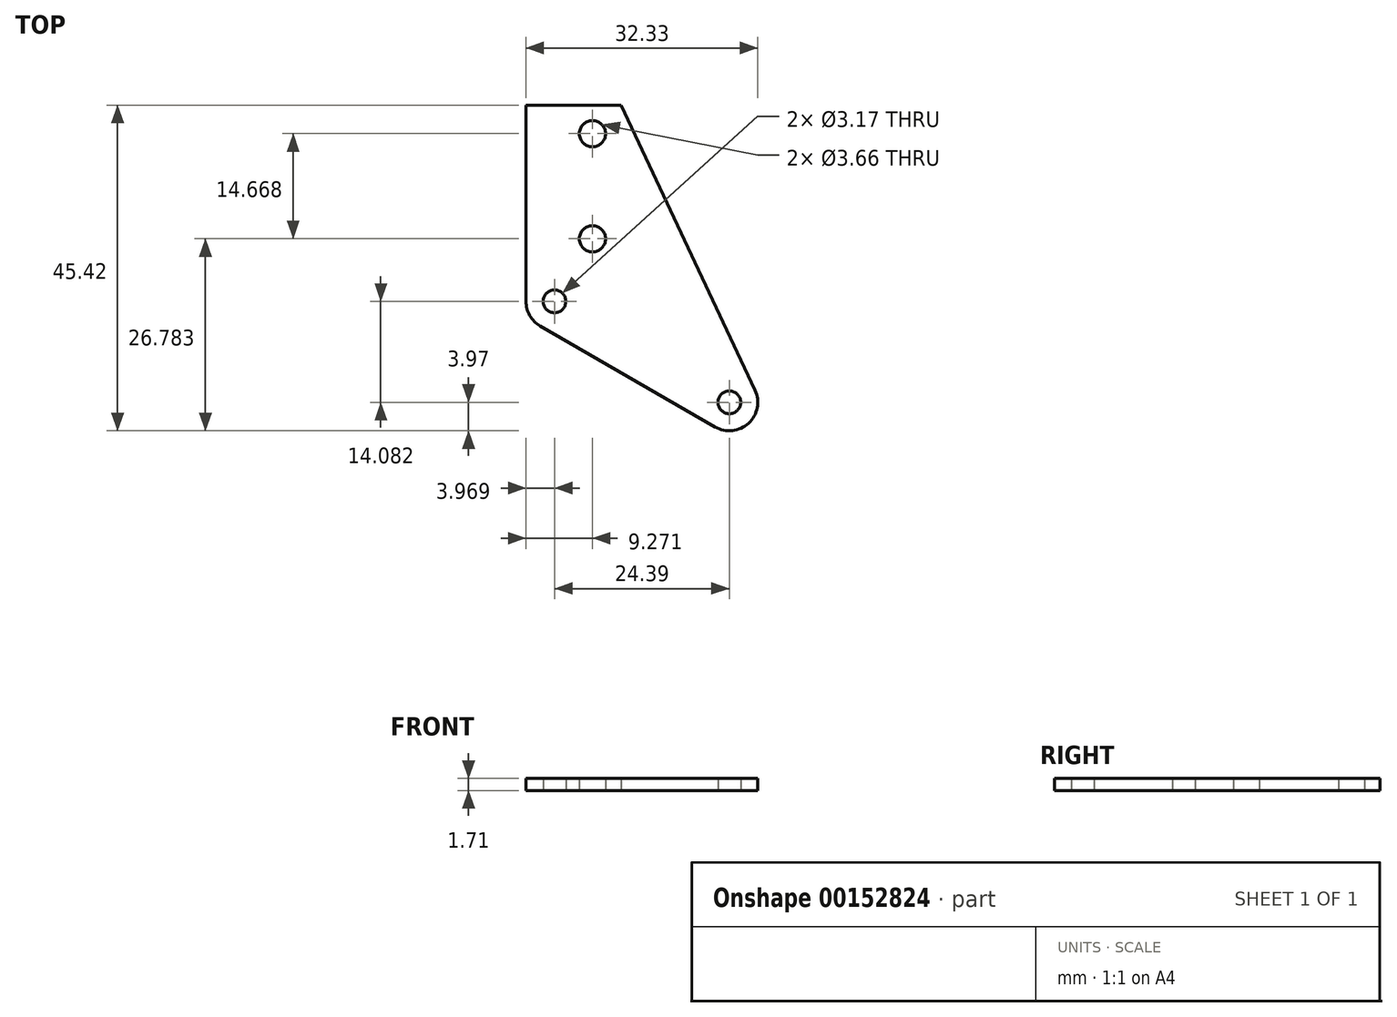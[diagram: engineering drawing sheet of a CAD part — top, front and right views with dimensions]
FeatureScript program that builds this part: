
annotation { "Feature Type Name" : "Feature", "Feature Type Description" : "" }
export const myFeature = defineFeature(function(context is Context, id is Id, definition is map)
    precondition{}
    {
        {
            var Q0;
            Q0=qCreatedBy(makeId("Top.planeOp"),FACE);
            var sketch = newSketch(context, id + "F0", { "sketchPlane" : qUnion([Q0])});
            skLineSegment(sketch, "E0", {"start": v(0, 0) * mm, "end": v(0, -27.37) * mm});
            skLineSegment(sketch, "E1", {"start": v(0, 0) * mm, "end": v(13.24, 0) * mm});
            skLineSegment(sketch, "E2", {"start": v(13.24, 0) * mm, "end": v(31.95, -39.76) * mm});
            skArc(sketch, "E3", {"start": v(0, -27.37) * mm, "mid": v(0.53, -29.35) * mm, "end": v(1.98, -30.8) * mm});
            skArc(sketch, "E4", {"start": v(26.37, -44.89) * mm, "mid": v(31.05, -44.37) * mm, "end": v(31.95, -39.76) * mm});
            skLineSegment(sketch, "E5", {"start": v(1.98, -30.8) * mm, "end": v(26.37, -44.89) * mm});
            skCircle(sketch, "E6", {"center": v(3.97, -27.37) * mm, "radius": 1.59 * mm});
            skCircle(sketch, "E7", {"center": v(28.36, -41.45) * mm, "radius": 1.59 * mm});
            skLineSegment(sketch, "E8", {"start": v(13.24, 0) * mm, "end": v(13.24, -3.97) * mm, "construction": true});
            skLineSegment(sketch, "E9", {"start": v(13.24, -3.97) * mm, "end": v(9.27, -3.97) * mm, "construction": true});
            skLineSegment(sketch, "E10", {"start": v(9.27, -3.97) * mm, "end": v(9.27, -18.64) * mm, "construction": true});
            skArc(sketch, "E11", {"start": v(3.97, -23.4) * mm, "mid": v(1.16, -24.56) * mm, "end": v(0, -27.37) * mm, "construction": true});
            skLineSegment(sketch, "E12", {"start": v(3.97, -23.4) * mm, "end": v(24.25, -23.4) * mm, "construction": true});
            skLineSegment(sketch, "E13", {"start": v(9.27, -18.64) * mm, "end": v(9.27, -23.4) * mm, "construction": true});
            skCircle(sketch, "E14", {"center": v(9.27, -3.97) * mm, "radius": 1.83 * mm});
            skCircle(sketch, "E15", {"center": v(9.27, -18.64) * mm, "radius": 1.83 * mm});
            skLineSegment(sketch, "E16", {"start": v(1.98, -30.8) * mm, "end": v(14.18, -30.8) * mm, "construction": true});
            skLineSegment(sketch, "E17", {"start": v(14.18, -30.8) * mm, "end": v(14.18, -37.85) * mm, "construction": true});
            skSolve(sketch);
        }
        {
            var Q0;
            Q0=makeQuery(id+"F0.imprint","IMPRINT",FACE,{"disambiguationData":[TD([[makeQuery(id+"F0.imprint","IMPRINT",EDGE,{"derivedFrom":sQuery(id+"F0.wireOp",EDGE,"E0")}),1.0]])]});
            extrude(context, id + "F1", {"entities" : qUnion([Q0]), "depth" : 1.7 * mm});
        }
    });
